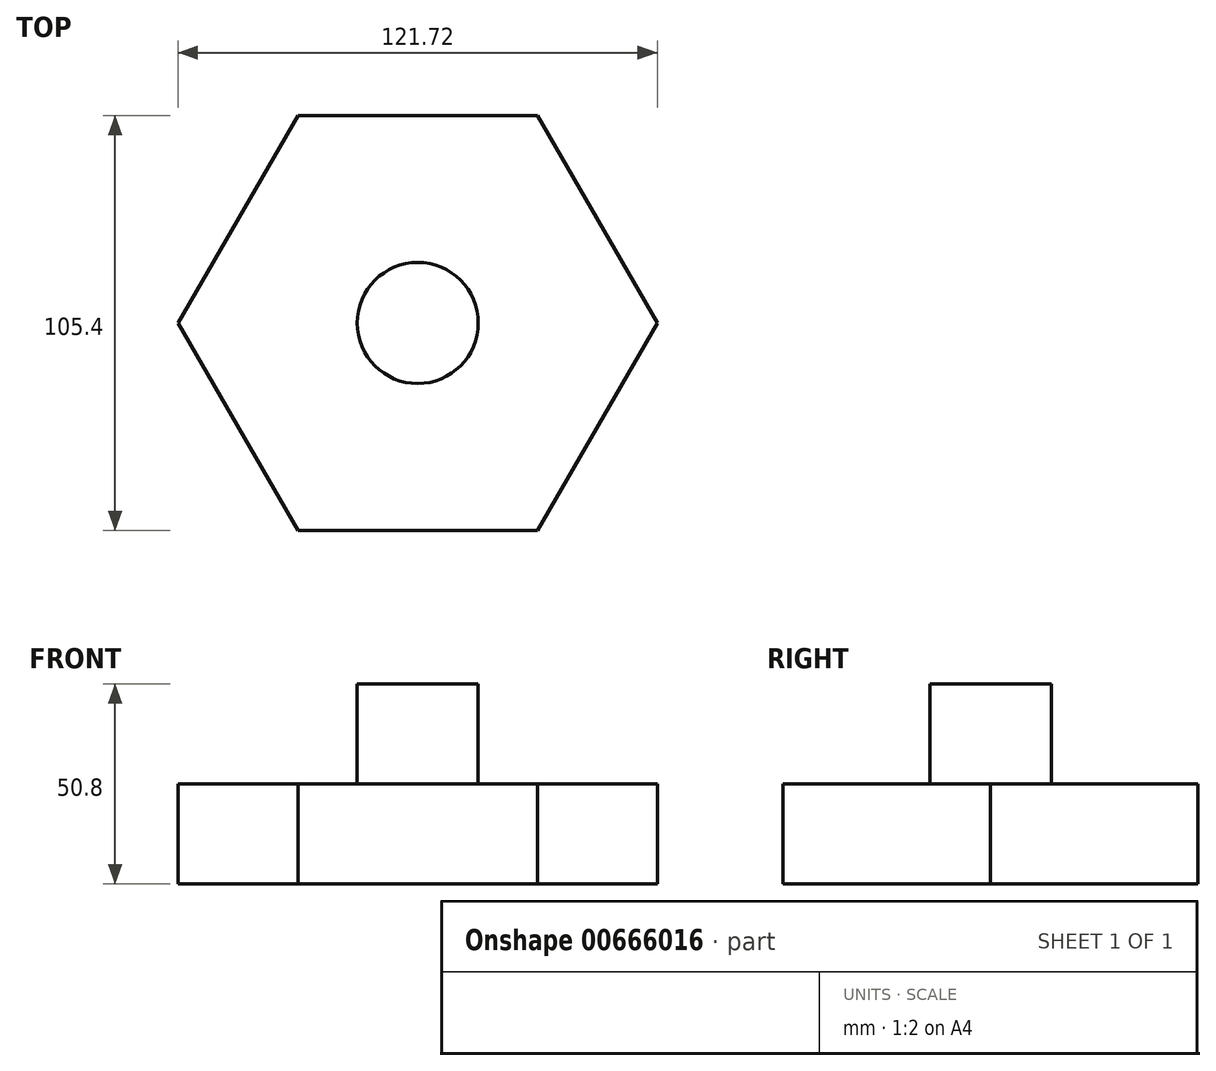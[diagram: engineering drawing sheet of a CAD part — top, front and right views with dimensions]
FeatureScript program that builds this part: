
annotation { "Feature Type Name" : "Feature", "Feature Type Description" : "" }
export const myFeature = defineFeature(function(context is Context, id is Id, definition is map)
    precondition{}
    {
        {
            var Q0;
            Q0=qCreatedBy(makeId("Top.planeOp"),FACE);
            var sketch = newSketch(context, id + "F0", { "sketchPlane" : qUnion([Q0])});
            skCircle(sketch, "E0.cCircle", {"center": v(0, 0) * mm, "radius": 52.7 * mm, "construction": true});
            skLineSegment(sketch, "E0.0", {"start": v(-30.43, 52.7) * mm, "end": v(30.43, 52.7) * mm});
            skLineSegment(sketch, "E0.1", {"start": v(30.43, 52.7) * mm, "end": v(60.86, 0) * mm});
            skLineSegment(sketch, "E0.2", {"start": v(60.86, 0) * mm, "end": v(30.43, -52.7) * mm});
            skLineSegment(sketch, "E0.3", {"start": v(30.43, -52.7) * mm, "end": v(-30.43, -52.7) * mm});
            skLineSegment(sketch, "E0.4", {"start": v(-30.43, -52.7) * mm, "end": v(-60.86, 0) * mm});
            skLineSegment(sketch, "E0.5", {"start": v(-60.86, 0) * mm, "end": v(-30.43, 52.7) * mm});
            skPoint(sketch, "E0.0.midPoint", {"position": v(0, 52.7) * mm});
            skSolve(sketch);
        }
        {
            var Q0;
            Q0 = qSketchRegion(id + "F0", true);
            extrude(context, id + "F1", {"entities" : qUnion([Q0]), "depth" : 25.4 * mm, "offsetDistance" : 25.4 * mm});
        }
        {
            var Q0;
            Q0=makeQuery(id+"F1.opExtrude","CAP_FACE",FACE,{"disambiguationData":[OSD([sQuery(id+"F0.wireOp",EDGE,"E0.0"),sQuery(id+"F0.wireOp",EDGE,"E0.1"),sQuery(id+"F0.wireOp",EDGE,"E0.2"),sQuery(id+"F0.wireOp",EDGE,"E0.3"),sQuery(id+"F0.wireOp",EDGE,"E0.4"),sQuery(id+"F0.wireOp",EDGE,"E0.5")])],"isStart":false});
            var sketch = newSketch(context, id + "F2", { "sketchPlane" : qUnion([Q0])});
            skCircle(sketch, "E1", {"center": v(0, 0) * mm, "radius": 15.38 * mm});
            skSolve(sketch);
        }
        {
            var Q0;
            Q0=makeQuery(id+"F2.imprint","IMPRINT",FACE,{"disambiguationData":[TD([[makeQuery(id+"F2.imprint","IMPRINT",EDGE,{"derivedFrom":sQuery(id+"F2.wireOp",EDGE,"E1")}),1.0]])]});
            extrude(context, id + "F3", {"entities" : qUnion([Q0]), "operationType" : NewBodyOperationType.ADD, "depth" : 25.4 * mm, "offsetDistance" : 25.4 * mm});
        }
    });
